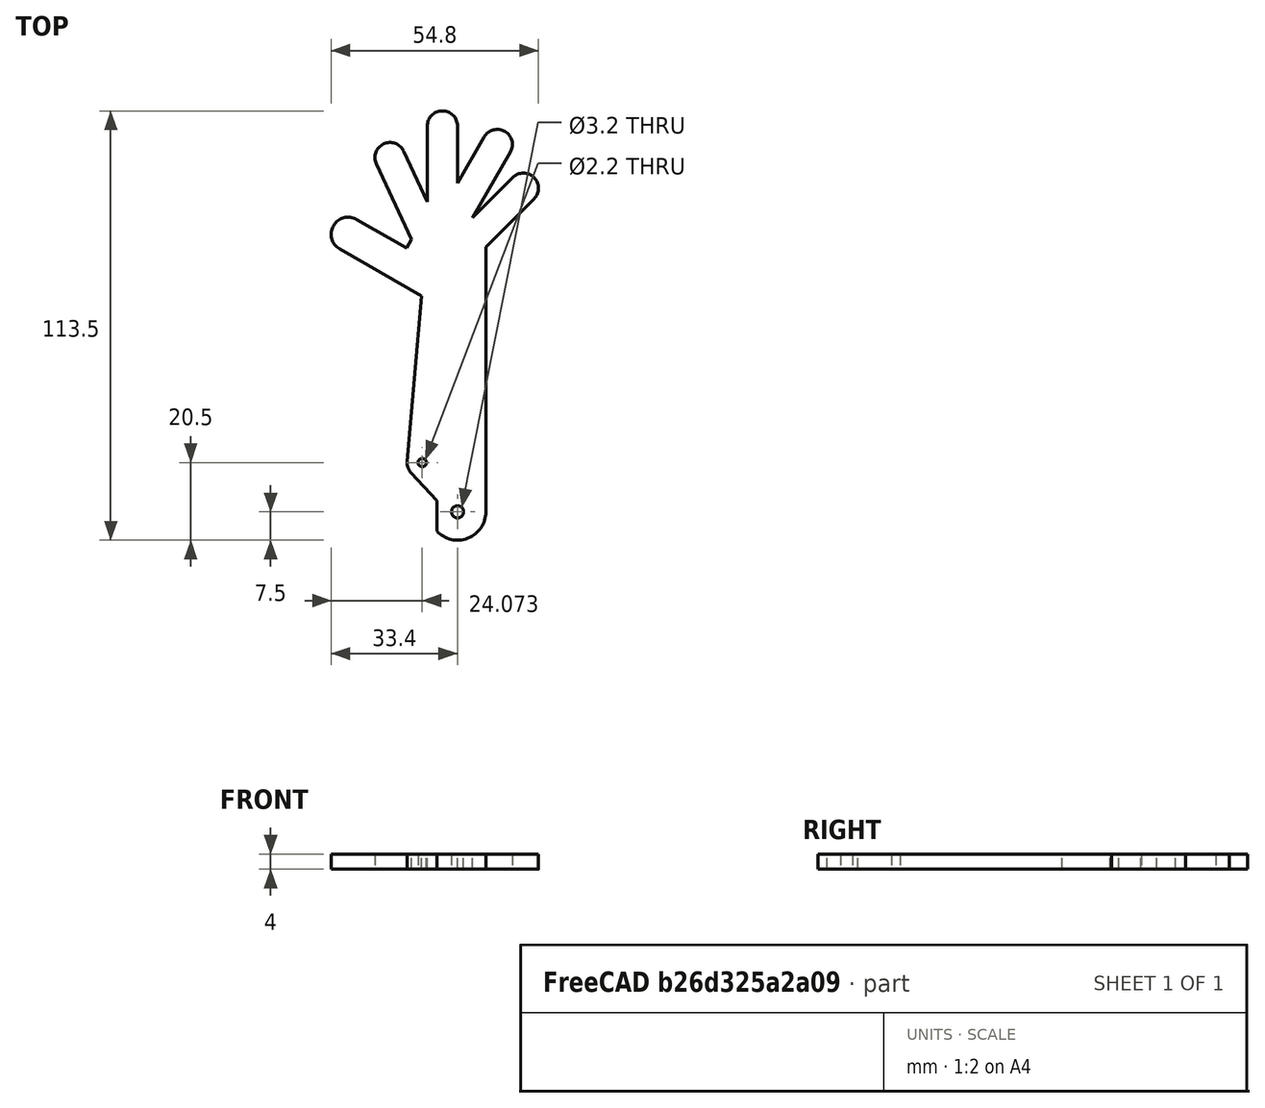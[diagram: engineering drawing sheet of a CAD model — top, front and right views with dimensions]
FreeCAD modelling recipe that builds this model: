
FCSTD DOCUMENT  (FreeCAD 0.21R33771 (Git))
Label: 4_Arms_Palm
License: All rights reserved
LicenseURL: http://en.wikipedia.org/wiki/All_rights_reserved
objects: Sketcher::SketchObject×1, PartDesign::Pad×1, PartDesign::Body×1
note: 4 computed .brp shape members not serialized (recipe doc carries the construction recipe); baked Part::Feature solids carry a one-line shape summary decoded from their .brp

FEATURE [Sketcher::SketchObject] Sketch
  FullyConstrained = true
  MapMode = 5
  Support = -> [XY_Plane]
  sketch-geometry (25):
    g0: LineSegment StartX=7.5 StartY=-1.8e-15 StartZ=0 EndX=7.5 EndY=70 EndZ=0
    g1: LineSegment StartX=-13.3122 StartY=13.348 StartZ=0 EndX=-9.5 EndY=57 EndZ=0
    g2: ArcOfCircle CenterX=0 CenterY=0 CenterZ=0 NormalX=0 NormalY=0 NormalZ=1 AngleXU=0 Radius=7.5 StartAngle=3.88918 EndAngle=6.28319
    g3: ArcOfCircle CenterX=-9.32738 CenterY=13 CenterZ=0 NormalX=0 NormalY=0 NormalZ=1 AngleXU=0 Radius=4 StartAngle=3.05448 EndAngle=3.88999
    g4: LineSegment StartX=-13.4932 StartY=69.6978 StartZ=0 EndX=-26.6506 EndY=77.2942 EndZ=0
    g5: LineSegment StartX=7.5 StartY=70 StartZ=0 EndX=20.2279 EndY=82.7279 EndZ=0
    g6: LineSegment StartX=-14.2111 StartY=95.3197 StartZ=0 EndX=-8 EndY=82 EndZ=0
    g7: LineSegment StartX=14.5711 StartY=88.3848 StartZ=0 EndX=3.96447 EndY=77.7782 EndZ=0
    g8: ArcOfCircle CenterX=-28.9006 CenterY=73.3971 CenterZ=0 NormalX=0 NormalY=0 NormalZ=1 AngleXU=0 Radius=4.5 StartAngle=1.0472 EndAngle=4.18879
    g9: LineSegment StartX=-9.32738 StartY=13 StartZ=0 EndX=0 EndY=0 EndZ=0
    g10: LineSegment StartX=-31.1506 StartY=69.5 StartZ=0 EndX=-9.5 EndY=57 EndZ=0
    g11: LineSegment StartX=-13.4932 StartY=69.6978 StartZ=0 EndX=-12.1639 EndY=72 EndZ=0
    g12: LineSegment StartX=-12.1639 StartY=72 StartZ=0 EndX=-21.4615 EndY=91.9388 EndZ=0
    g13: LineSegment StartX=-8 StartY=82 StartZ=0 EndX=-8 EndY=102 EndZ=0
    g14: LineSegment StartX=0 StartY=86.9115 StartZ=0 EndX=0 EndY=102 EndZ=0
    g15: LineSegment StartX=0 StartY=86.9115 StartZ=0 EndX=7.03626 EndY=99.0987 EndZ=0
    g16: LineSegment StartX=3.96447 StartY=77.7782 StartZ=0 EndX=13.9645 EndY=95.0987 EndZ=0
    g17: ArcOfCircle CenterX=17.3995 CenterY=85.5563 CenterZ=0 NormalX=0 NormalY=0 NormalZ=1 AngleXU=0 Radius=4 StartAngle=5.49779 EndAngle=8.63938
    g18: ArcOfCircle CenterX=-17.8363 CenterY=93.6292 CenterZ=0 NormalX=0 NormalY=0 NormalZ=1 AngleXU=0 Radius=4 StartAngle=0.436332 EndAngle=3.57792
    g19: ArcOfCircle CenterX=10.5004 CenterY=97.0987 CenterZ=0 NormalX=0 NormalY=0 NormalZ=1 AngleXU=0 Radius=4 StartAngle=5.75959 EndAngle=8.90118
    g20: ArcOfCircle CenterX=-4 CenterY=102 CenterZ=0 NormalX=0 NormalY=0 NormalZ=1 AngleXU=0 Radius=4 StartAngle=1.7e-15 EndAngle=3.14159
    g21: Circle CenterX=0 CenterY=0 CenterZ=0 NormalX=0 NormalY=0 NormalZ=1 AngleXU=0 Radius=1.6
    g22: Circle CenterX=-9.32738 CenterY=13 CenterZ=0 NormalX=0 NormalY=0 NormalZ=1 AngleXU=0 Radius=1.1
    g23: LineSegment StartX=-12.2585 StartY=10.2781 StartZ=0 EndX=-5.5 EndY=3 EndZ=0
    g24: LineSegment StartX=-5.5 StartY=3 StartZ=0 EndX=-5.5 EndY=-5.09902 EndZ=0
  constraints (66):
    c: Tangent(g2,g0) = -1.5708
    c: Coincident(g2,g-1)
    c: Coincident(g5,g0)
    c: DistanceY(g2,g1) = 57
    c: Diameter(g2) = 15
    c: Distance(g2,g3) = 16
    c: Coincident(g9,g3)
    c: Coincident(g9,g2)
    c: Radius(g3) = 4
    c: PointOnObject(g0,g-1)
    c: DistanceY(g1,g0) = 13
    c: Coincident(g10,g1)
    c: Parallel(g4,g10)
    c: Tangent(g10,g8) = -1.5708
    c: Tangent(g8,g4) = -1.5708
    c: Distance(g10) = 25
    c: Coincident(g11,g4)
    c: Coincident(g12,g11)
    c: Coincident(g13,g6)
    c: Vertical(g14)
    c: Coincident(g15,g14)
    c: Coincident(g16,g7)
    c: Tangent(g1,g3) = 1.5708
    c: DistanceX(g1,g0) = 17
    c: PointOnObject(g14,g-2)
    c: Parallel(g7,g5)
    c: Diameter(g8) = 9
    c: DistanceY(g1,g14) = 45
    c: Vertical(g13)
    c: Distance(g5) = 18
    c: Parallel(g16,g15)
    c: Distance(g16) = 20
    c: Tangent(g17,g7) = -1.5708
    c: Tangent(g17,g5) = -1.5708
    c: Diameter(g17) = 8
    c: Parallel(g12,g6)
    c: Tangent(g18,g12) = 1.5708
    c: Tangent(g18,g6) = 1.5708
    c: Diameter(g18) = 8
    c: Angle(g10,g-2) = 2.0944
    c: Angle(g12,g-2) = 2.70526
    c: Distance(g12) = 22
    c: Angle(g-2,g5) = 2.35619
    c: Tangent(g19,g15) = 1.5708
    c: Tangent(g19,g16) = -1.5708
    c: Diameter(g19) = 8
    c: Tangent(g20,g13) = 1.5708
    c: Tangent(g20,g14) = -1.5708
    c: Diameter(g20) = 8
    c: Angle(g-2,g16) = 2.61799
    c: Distance(g7) = 15
    c: Perpendicular(g11,g4)
    c: Diameter(g21) = 3.2
    c: Coincident(g21,g2)
    c: Diameter(g22) = 2.2
    c: Coincident(g3,g22)
    c: DistanceX(g3,g2) = 9.32738
    c: Coincident(g24,g23)
    c: Coincident(g24,g2)
    c: Vertical(g24)
    c: DistanceX(g23,g0) = 13
    c: DistanceY(g2,g3) = 13
    c: DistanceY(g0,g23) = 3
    c: Tangent(g23,g3) = -1.5708
    c: DistanceY(g1,g6) = 25
    c: DistanceY(g1,g11) = 15
FEATURE [PartDesign::Pad] Pad
  Direction = (0,0,1)
  Length = 4
  Length2 = 10
  Profile = -> Sketch
  ReferenceAxis = -> Sketch [N_Axis]
  Type = 0
FEATURE [PartDesign::Body] Body
  Group = -> [Sketch,Pad]
  Origin = -> Origin
  Tip = -> Pad
